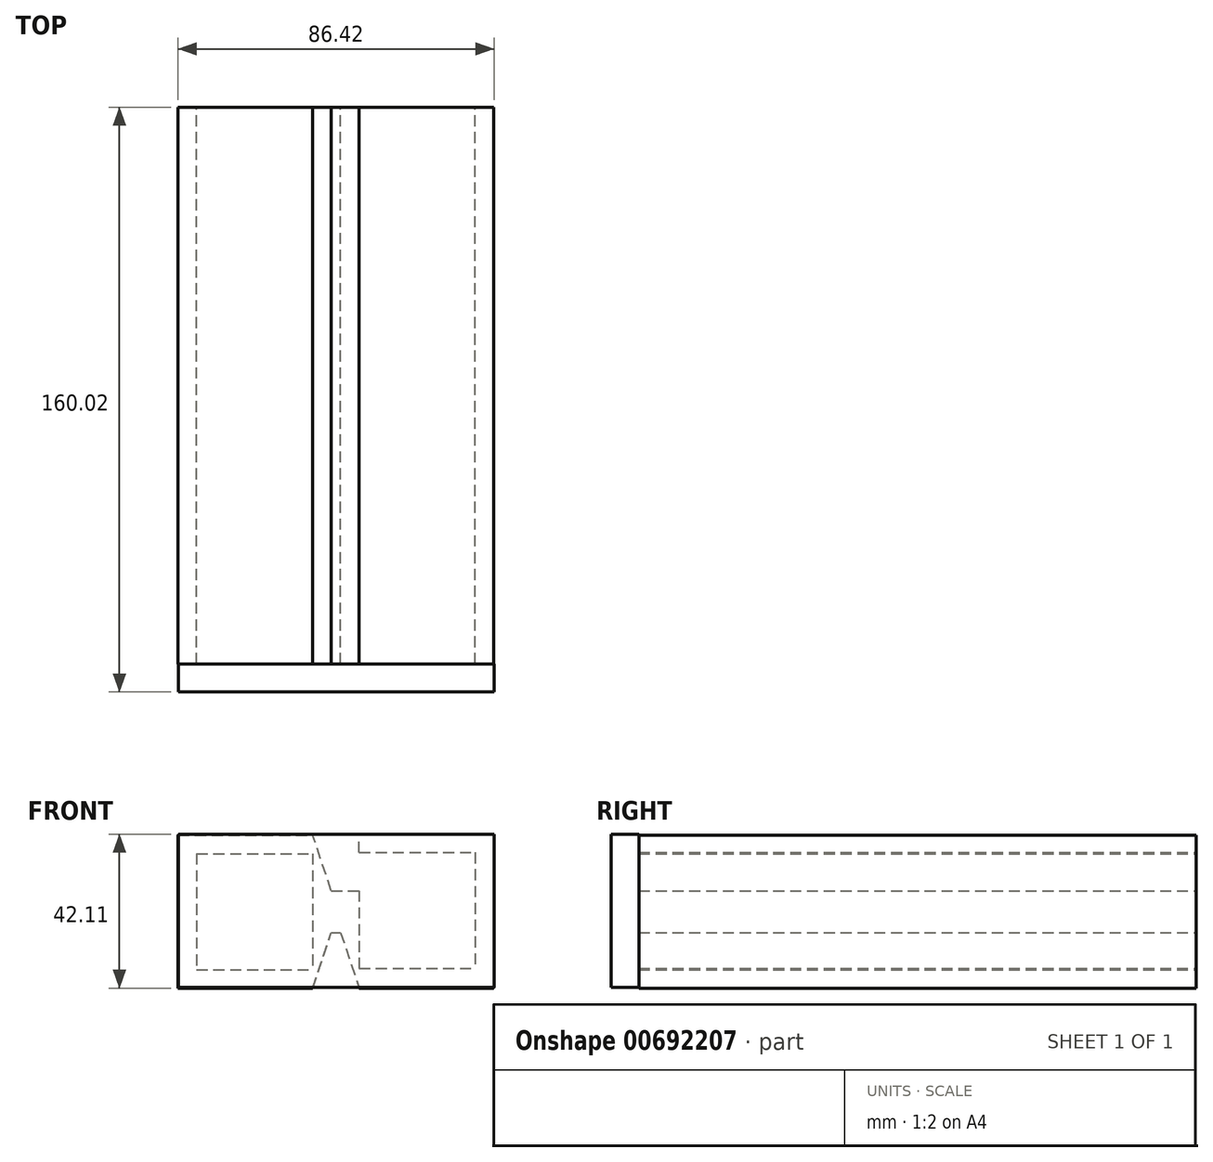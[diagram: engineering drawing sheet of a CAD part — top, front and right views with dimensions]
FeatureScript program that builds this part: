
annotation { "Feature Type Name" : "Feature", "Feature Type Description" : "" }
export const myFeature = defineFeature(function(context is Context, id is Id, definition is map)
    precondition{}
    {
        {
            var Q0;
            Q0=qCreatedBy(makeId("Front.planeOp"),FACE);
            var sketch = newSketch(context, id + "F0", { "sketchPlane" : qUnion([Q0])});
            skLineSegment(sketch, "E0.bottom", {"start": v(-39.37, 40.12) * mm, "end": v(-7.62, 40.12) * mm});
            skLineSegment(sketch, "E0.top", {"start": v(-39.37, 8.37) * mm, "end": v(-7.62, 8.37) * mm});
            skLineSegment(sketch, "E0.left", {"start": v(-39.37, 40.12) * mm, "end": v(-39.37, 8.37) * mm});
            skLineSegment(sketch, "E0.right", {"start": v(-7.62, 40.12) * mm, "end": v(-7.62, 8.37) * mm});
            skLineSegment(sketch, "E1.bottom", {"start": v(5.08, 40.42) * mm, "end": v(36.83, 40.42) * mm});
            skLineSegment(sketch, "E1.top", {"start": v(5.08, 8.67) * mm, "end": v(36.83, 8.67) * mm});
            skLineSegment(sketch, "E1.left", {"start": v(5.08, 40.42) * mm, "end": v(5.08, 8.67) * mm});
            skLineSegment(sketch, "E1.right", {"start": v(36.83, 40.42) * mm, "end": v(36.83, 8.67) * mm});
            skLineSegment(sketch, "E2", {"start": v(-7.62, 29.96) * mm, "end": v(5.08, 29.96) * mm});
            skLineSegment(sketch, "E3", {"start": v(-7.62, 18.53) * mm, "end": v(5.08, 18.53) * mm});
            skLineSegment(sketch, "E4", {"start": v(-39.37, 40.12) * mm, "end": v(-44.45, 40.12) * mm});
            skLineSegment(sketch, "E5", {"start": v(-44.45, 40.12) * mm, "end": v(-44.45, 8.37) * mm});
            skLineSegment(sketch, "E6", {"start": v(-44.45, 8.37) * mm, "end": v(-39.37, 8.37) * mm});
            skLineSegment(sketch, "E7", {"start": v(-39.37, 8.37) * mm, "end": v(-39.37, 3.3) * mm});
            skLineSegment(sketch, "E8", {"start": v(-44.45, 8.37) * mm, "end": v(-44.45, 3.3) * mm});
            skLineSegment(sketch, "E9", {"start": v(-44.45, 3.3) * mm, "end": v(-39.37, 3.3) * mm});
            skLineSegment(sketch, "E10", {"start": v(-7.62, 3.3) * mm, "end": v(-39.37, 3.3) * mm});
            skLineSegment(sketch, "E11", {"start": v(-7.62, 3.3) * mm, "end": v(-7.62, 8.37) * mm});
            skLineSegment(sketch, "E12", {"start": v(-7.62, 3.3) * mm, "end": v(-2.54, 3.3) * mm});
            skLineSegment(sketch, "E13", {"start": v(-2.54, 3.3) * mm, "end": v(-2.54, 18.53) * mm});
            skLineSegment(sketch, "E14", {"start": v(-39.37, 40.12) * mm, "end": v(-39.37, 45.2) * mm});
            skLineSegment(sketch, "E15", {"start": v(-39.37, 45.2) * mm, "end": v(-44.45, 45.2) * mm});
            skLineSegment(sketch, "E16", {"start": v(-44.45, 45.2) * mm, "end": v(-44.45, 40.12) * mm});
            skLineSegment(sketch, "E17", {"start": v(-39.37, 45.2) * mm, "end": v(-2.54, 45.2) * mm});
            skLineSegment(sketch, "E18", {"start": v(-2.54, 45.2) * mm, "end": v(-2.54, 29.96) * mm});
            skLineSegment(sketch, "E19", {"start": v(-2.54, 29.96) * mm, "end": v(-2.54, 18.53) * mm});
            skLineSegment(sketch, "E20", {"start": v(5.08, 40.42) * mm, "end": v(5.08, 45.2) * mm});
            skLineSegment(sketch, "E21", {"start": v(5.08, 45.2) * mm, "end": v(5.08, 40.42) * mm});
            skLineSegment(sketch, "E22", {"start": v(5.08, 45.2) * mm, "end": v(0, 45.2) * mm});
            skLineSegment(sketch, "E23", {"start": v(0, 45.2) * mm, "end": v(0, 29.96) * mm});
            skLineSegment(sketch, "E24", {"start": v(0, 18.53) * mm, "end": v(0, 3.3) * mm});
            skLineSegment(sketch, "E25", {"start": v(0, 3.3) * mm, "end": v(36.83, 3.3) * mm});
            skLineSegment(sketch, "E26", {"start": v(36.83, 3.3) * mm, "end": v(36.83, 8.67) * mm});
            skLineSegment(sketch, "E27", {"start": v(36.83, 8.67) * mm, "end": v(41.91, 8.67) * mm});
            skLineSegment(sketch, "E28", {"start": v(41.91, 8.67) * mm, "end": v(41.91, 3.3) * mm});
            skLineSegment(sketch, "E29", {"start": v(41.91, 3.3) * mm, "end": v(36.83, 3.3) * mm});
            skLineSegment(sketch, "E30", {"start": v(41.91, 8.67) * mm, "end": v(41.91, 45.2) * mm});
            skLineSegment(sketch, "E31", {"start": v(41.91, 45.2) * mm, "end": v(5.08, 45.2) * mm});
            skLineSegment(sketch, "E32", {"start": v(0, 29.96) * mm, "end": v(0, 18.53) * mm});
            skLineSegment(sketch, "E33", {"start": v(5.08, 8.67) * mm, "end": v(5.08, 3.3) * mm});
            skLineSegment(sketch, "E34", {"start": v(5.08, 8.67) * mm, "end": v(0, 8.67) * mm});
            skLineSegment(sketch, "E35", {"start": v(0, 29.96) * mm, "end": v(5.08, 45.2) * mm});
            skLineSegment(sketch, "E36", {"start": v(-7.62, 40.12) * mm, "end": v(-7.62, 45.2) * mm});
            skLineSegment(sketch, "E37", {"start": v(-7.62, 3.3) * mm, "end": v(-2.54, 18.53) * mm});
            skLineSegment(sketch, "E38", {"start": v(0, 18.53) * mm, "end": v(5.08, 3.3) * mm});
            skLineSegment(sketch, "E39", {"start": v(-2.54, 29.96) * mm, "end": v(-7.62, 45.2) * mm});
            skSolve(sketch);
        }
        {
            var Q0;
            {var subQ1=sQuery(id+"F0.wireOp",EDGE,"E1.top");Q0=makeQuery(id+"F0.imprint","IMPRINT",FACE,{"disambiguationData":[TD([[makeQuery(id+"F0.imprint","IMPRINT",EDGE,{"derivedFrom":subQ1}),-1.0]])]});}
            var Q1;
            {var subQ0=sQuery(id+"F0.wireOp",EDGE,"E19");Q1=makeQuery(id+"F0.imprint","IMPRINT",FACE,{"disambiguationData":[TD([[makeQuery(id+"F0.imprint","IMPRINT",EDGE,{"derivedFrom":subQ0}),1.0]])]});}
            var Q2;
            {var subQ0=sQuery(id+"F0.wireOp",EDGE,"E21");Q2=makeQuery(id+"F0.imprint","IMPRINT",FACE,{"disambiguationData":[TD([[makeQuery(id+"F0.imprint","IMPRINT",EDGE,{"derivedFrom":subQ0}),-1.0]])]});}
            var Q3;
            Q3=makeQuery(id+"F0.imprint","IMPRINT",FACE,{"disambiguationData":[TD([[makeQuery(id+"F0.imprint","IMPRINT",EDGE,{"derivedFrom":sQuery(id+"F0.wireOp",EDGE,"E1.bottom")}),1.0]])]});
            var Q4;
            Q4=makeQuery(id+"F0.imprint","IMPRINT",FACE,{"disambiguationData":[TD([[makeQuery(id+"F0.imprint","IMPRINT",EDGE,{"derivedFrom":sQuery(id+"F0.wireOp",EDGE,"E26")}),-1.0]])]});
            var Q5;
            {var subQ5=sQuery(id+"F0.wireOp",EDGE,"E19");Q5=makeQuery(id+"F0.imprint","IMPRINT",FACE,{"disambiguationData":[TD([[makeQuery(id+"F0.imprint","IMPRINT",EDGE,{"derivedFrom":subQ5}),-1.0]])]});}
            var Q6;
            {var subQ4=sQuery(id+"F0.wireOp",EDGE,"E0.bottom");Q6=makeQuery(id+"F0.imprint","IMPRINT",FACE,{"disambiguationData":[TD([[makeQuery(id+"F0.imprint","IMPRINT",EDGE,{"derivedFrom":subQ4}),1.0]])]});}
            var Q7;
            Q7=makeQuery(id+"F0.imprint","IMPRINT",FACE,{"disambiguationData":[TD([[makeQuery(id+"F0.imprint","IMPRINT",EDGE,{"derivedFrom":sQuery(id+"F0.wireOp",EDGE,"E4")}),-1.0]])]});
            var Q8;
            Q8=makeQuery(id+"F0.imprint","IMPRINT",FACE,{"disambiguationData":[TD([[makeQuery(id+"F0.imprint","IMPRINT",EDGE,{"derivedFrom":sQuery(id+"F0.wireOp",EDGE,"E0.left")}),-1.0]])]});
            var Q9;
            Q9=makeQuery(id+"F0.imprint","IMPRINT",FACE,{"disambiguationData":[TD([[makeQuery(id+"F0.imprint","IMPRINT",EDGE,{"derivedFrom":sQuery(id+"F0.wireOp",EDGE,"E6")}),-1.0]])]});
            var Q10;
            Q10=makeQuery(id+"F0.imprint","IMPRINT",FACE,{"disambiguationData":[TD([[makeQuery(id+"F0.imprint","IMPRINT",EDGE,{"derivedFrom":sQuery(id+"F0.wireOp",EDGE,"E0.top")}),-1.0]])]});
            var Q11;
            {var subQ4=sQuery(id+"F0.wireOp",EDGE,"E11");Q11=makeQuery(id+"F0.imprint","IMPRINT",FACE,{"disambiguationData":[TD([[makeQuery(id+"F0.imprint","IMPRINT",EDGE,{"derivedFrom":subQ4}),-1.0]])]});}
            var Q12;
            {var subQ5=sQuery(id+"F0.wireOp",EDGE,"E32");Q12=makeQuery(id+"F0.imprint","IMPRINT",FACE,{"disambiguationData":[TD([[makeQuery(id+"F0.imprint","IMPRINT",EDGE,{"derivedFrom":subQ5}),1.0]])]});}
            var Q13;
            {var subQ4=sQuery(id+"F0.wireOp",EDGE,"E33");Q13=makeQuery(id+"F0.imprint","IMPRINT",FACE,{"disambiguationData":[TD([[makeQuery(id+"F0.imprint","IMPRINT",EDGE,{"derivedFrom":subQ4}),-1.0]])]});}
            var Q14;
            {var subQ1=sQuery(id+"F0.wireOp",EDGE,"E1.left");var subQ3=sQuery(id+"F0.wireOp",EDGE,"E3");var subQ4=makeQuery(id+"F0.imprint","INTERSECT",VERTEX,{"derivedFrom":[subQ1,subQ3]});Q14=makeQuery(id+"F0.imprint","IMPRINT",FACE,{"disambiguationData":[TD([[makeQuery(id+"F0.imprint","IMPRINT",EDGE,{"disambiguationData":[TD([[subQ4,-1.0]])],"derivedFrom":subQ1}),-1.0]])]});}
            var Q15;
            {var subQ0=sQuery(id+"F0.wireOp",EDGE,"E36");Q15=makeQuery(id+"F0.imprint","IMPRINT",FACE,{"disambiguationData":[TD([[makeQuery(id+"F0.imprint","IMPRINT",EDGE,{"derivedFrom":subQ0}),-1.0]])]});}
            extrude(context, id + "F1", {"entities" : qUnion([Q0, Q1, Q2, Q3, Q4, Q5, Q6, Q7, Q8, Q9, Q10, Q11, Q12, Q13, Q14, Q15]), "depth" : 152.4 * mm, "offsetDistance" : 25.4 * mm});
        }
        {
            var Q0;
            Q0=qCreatedBy(makeId("Front.planeOp"),FACE);
            cPlane(context, id + "F2", {"entities" : qUnion([Q0]), "cplaneType" : CPlaneType.OFFSET, "offset" : 152.4 * mm, "width" : 152.4 * mm, "height" : 152.4 * mm});
        }
        {
            var Q0;
            Q0=qCreatedBy(id+"F2.planeOp",FACE);
            var sketch = newSketch(context, id + "F3", { "sketchPlane" : qUnion([Q0])});
            skLineSegment(sketch, "E40.bottom", {"start": v(-44.39, 45.4) * mm, "end": v(41.97, 45.4) * mm});
            skLineSegment(sketch, "E40.top", {"start": v(-44.39, 3.49) * mm, "end": v(41.97, 3.49) * mm});
            skLineSegment(sketch, "E40.left", {"start": v(-44.39, 45.4) * mm, "end": v(-44.39, 3.49) * mm});
            skLineSegment(sketch, "E40.right", {"start": v(41.97, 45.4) * mm, "end": v(41.97, 3.49) * mm});
            skSolve(sketch);
        }
        {
            var Q0;
            Q0 = qSketchRegion(id + "F3", true);
            extrude(context, id + "F4", {"entities" : qUnion([Q0]), "operationType" : NewBodyOperationType.ADD, "depth" : 7.62 * mm, "offsetDistance" : 25.4 * mm});
        }
    });
